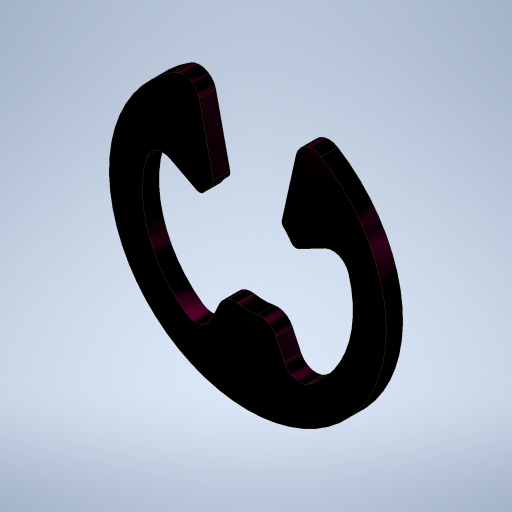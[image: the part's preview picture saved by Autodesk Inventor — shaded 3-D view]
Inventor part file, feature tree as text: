
AUTODESK INVENTOR PART (.ipt)
format: ipt  version: 2023.1 (Build 271208000, 208)  size: 308,736 bytes
history: native  units: in
note: dims shown in document units (in); Inventor stores cm internally (conversion verified against a paired STEP export)
features: extrude x3, sketch x3, fillet x2, projected_geometry x1
ambient origin geometry x8: Origin, YZ Plane, XZ Plane, XY Plane, X Axis, Y Axis, Z Axis, Center Point
bodies: Solid1 (feature_tree)
feature tree (9):
  extrude  "Extrusion1"  Depth=0.25in
  extrude  "Extrusion2"  Depth=0.015in
  extrude  "Extrusion3"  Depth=0.005in
  fillet  "Fillet1"  Radius=0.015in
  fillet  "Fillet2"  Radius=0.03in
  sketch  "Sketch1"  dims[d0=0.0938in d1=0.25in]
  sketch  "Sketch2"  dims[d2=0.015in d3=0.0in d4=0.05in]
  sketch  "Sketch3"  dims[d5=0.1in d6=0.1718in d7=0.015in d8=0.0in d9=0.03in d10=0.3436in d11=0.3436in d12=0.0832in d13=0.0396in d14=0.015in d15=0.0in d16=0.015in d17=0.005in]
  projected_geometry  "Project Cut Edges1"
